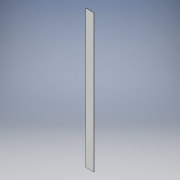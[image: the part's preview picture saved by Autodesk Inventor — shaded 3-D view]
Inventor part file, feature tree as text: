
AUTODESK INVENTOR PART (.ipt)
format: ipt  version: 2019 (Build 230136000, 136)  size: 92,672 bytes
history: native  units: in
note: dims shown in document units (in); Inventor stores cm internally (conversion verified against a paired STEP export)
features: extrude x1, sketch x1
ambient origin geometry x8: Origin, YZ Plane, XZ Plane, XY Plane, X Axis, Y Axis, Z Axis, Center Point
bodies: Solid1 (feature_tree)
feature tree (2):
  extrude  "Extrusion1"  Depth=1.976in
  sketch  "Sketch1"  dims[d0=0.115in d1=1.976in d2=0.005in d3=0.0in]
